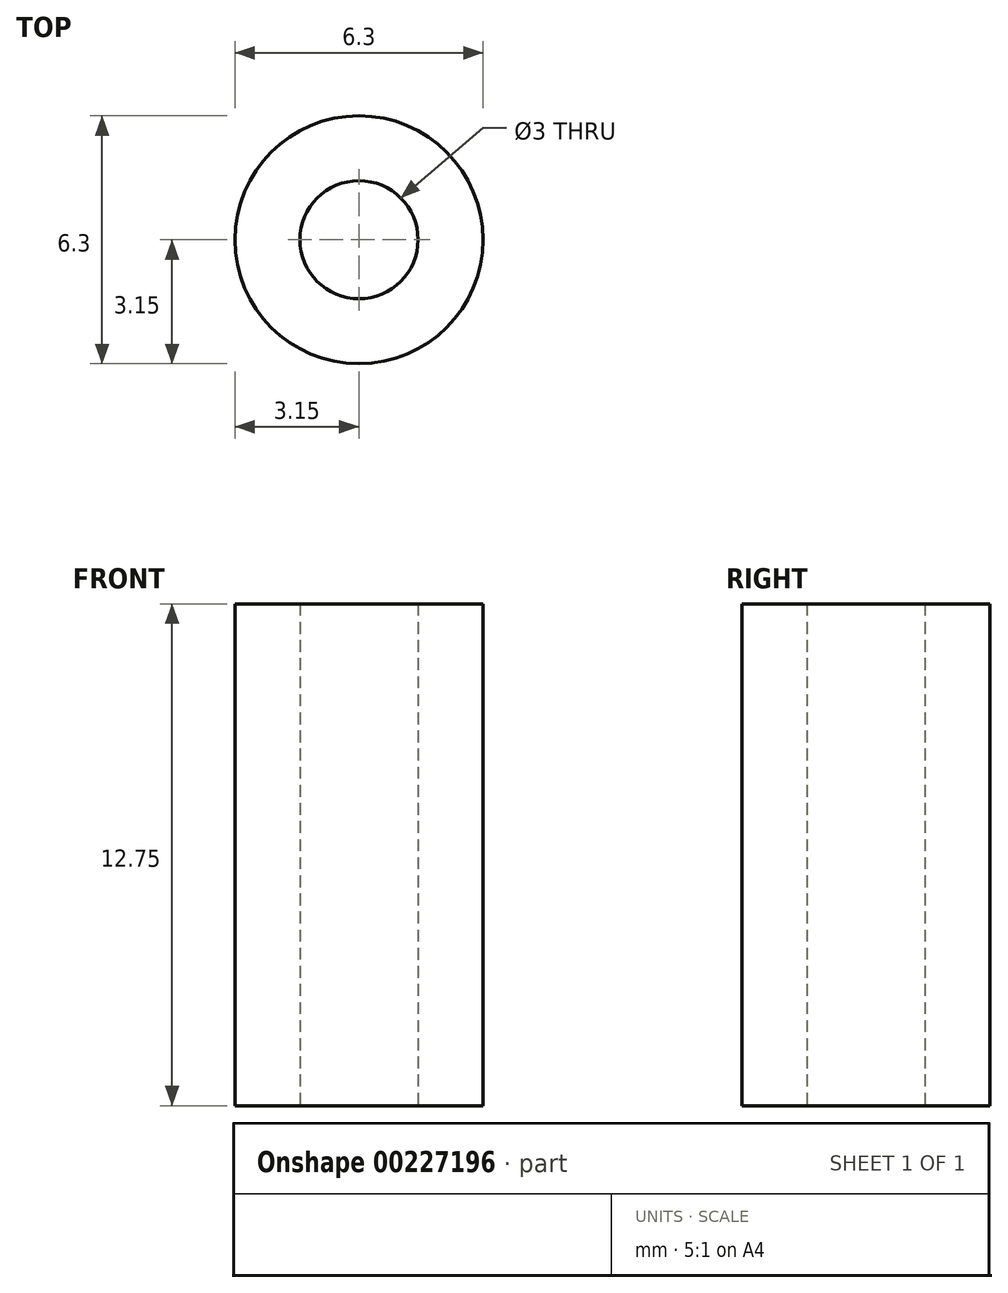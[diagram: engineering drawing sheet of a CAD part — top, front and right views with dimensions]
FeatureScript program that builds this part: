
annotation { "Feature Type Name" : "Feature", "Feature Type Description" : "" }
export const myFeature = defineFeature(function(context is Context, id is Id, definition is map)
    precondition{}
    {
        {
            var Q0;
            Q0=qCreatedBy(makeId("Top.planeOp"),FACE);
            var sketch = newSketch(context, id + "F0", { "sketchPlane" : qUnion([Q0])});
            skCircle(sketch, "E0", {"center": v(0, 0) * mm, "radius": 1.5 * mm});
            skCircle(sketch, "E1", {"center": v(0, 0) * mm, "radius": 3.15 * mm});
            skSolve(sketch);
        }
        {
            var Q0;
            Q0 = qSketchRegion(id + "F0", true);
            extrude(context, id + "F1", {"entities" : qUnion([Q0]), "depth" : 12.75 * mm});
        }
    });
